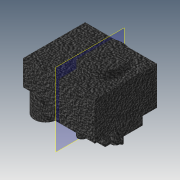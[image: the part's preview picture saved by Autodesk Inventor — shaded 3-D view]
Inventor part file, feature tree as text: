
AUTODESK INVENTOR PART (.ipt)
format: ipt  version: 2022 (Build 260153000, 153)  size: 229,888 bytes
history: native  units: mm
features: extrude x7, sketch x7, projected_geometry x2, plane x1
ambient origin geometry x8: Origin, YZ Plane, XZ Plane, XY Plane, X Axis, Y Axis, Z Axis, Center Point
bodies: Solid1 (feature_tree)
feature tree (17):
  extrude  "Extrusion1"  Depth=26.4mm
  extrude  "Extrusion2"  Depth=17.0mm
  extrude  "Extrusion3"  Depth=11.5mm
  extrude  "Extrusion4"  Depth=9.6mm
  extrude  "Extrusion5"  Depth=5.5mm TaperAngle=0.0deg
  extrude  "Extrusion6"  Depth=9.6mm TaperAngle=0.0deg
  extrude  "Extrusion7"  Depth=16.0mm
  plane  "Arbeitsebene1"
  sketch  "Sketch1"  dims[d0=30.5mm d1=26.4mm]
  sketch  "Sketch2"  dims[d2=16.2mm d3=0.0mm d4=17.0mm]
  sketch  "Sketch3"  dims[d5=11.5mm d6=11.5mm]
  sketch  "Sketch4"  dims[d7=3.5mm d8=0.0mm d9=9.6mm]
  projected_geometry  "Projected Loop1"
  sketch  "Sketch5"  dims[d10=9.6mm d11=5.5mm d12=0.0mm]
  sketch  "Sketch6"  dims[d13=9.6mm d14=9.6mm d15=0.0mm]
  projected_geometry  "Projected Loop2"
  sketch  "Sketch7"  dims[d16=17.0mm d17=16.0mm d18=3.5mm d19=2.5mm d20=2.0mm d21=6.0mm d22=0.0mm d23=3.5mm d24=3.5mm d25=3.5mm d26=3.5mm d27=11.5mm d28=3.0mm d29=9.0mm d30=10.0mm d31=11.5mm d32=6.0mm d33=2.2mm d34=15.5mm d35=1.8mm d36=1.8mm d37=1.8mm d38=6.0mm d39=0.0mm d40=1.3mm d41=1.3mm d42=12.0mm d43=3.0mm d44=4.5mm d45=20.5mm d46=8.7mm d47=0.0mm]
